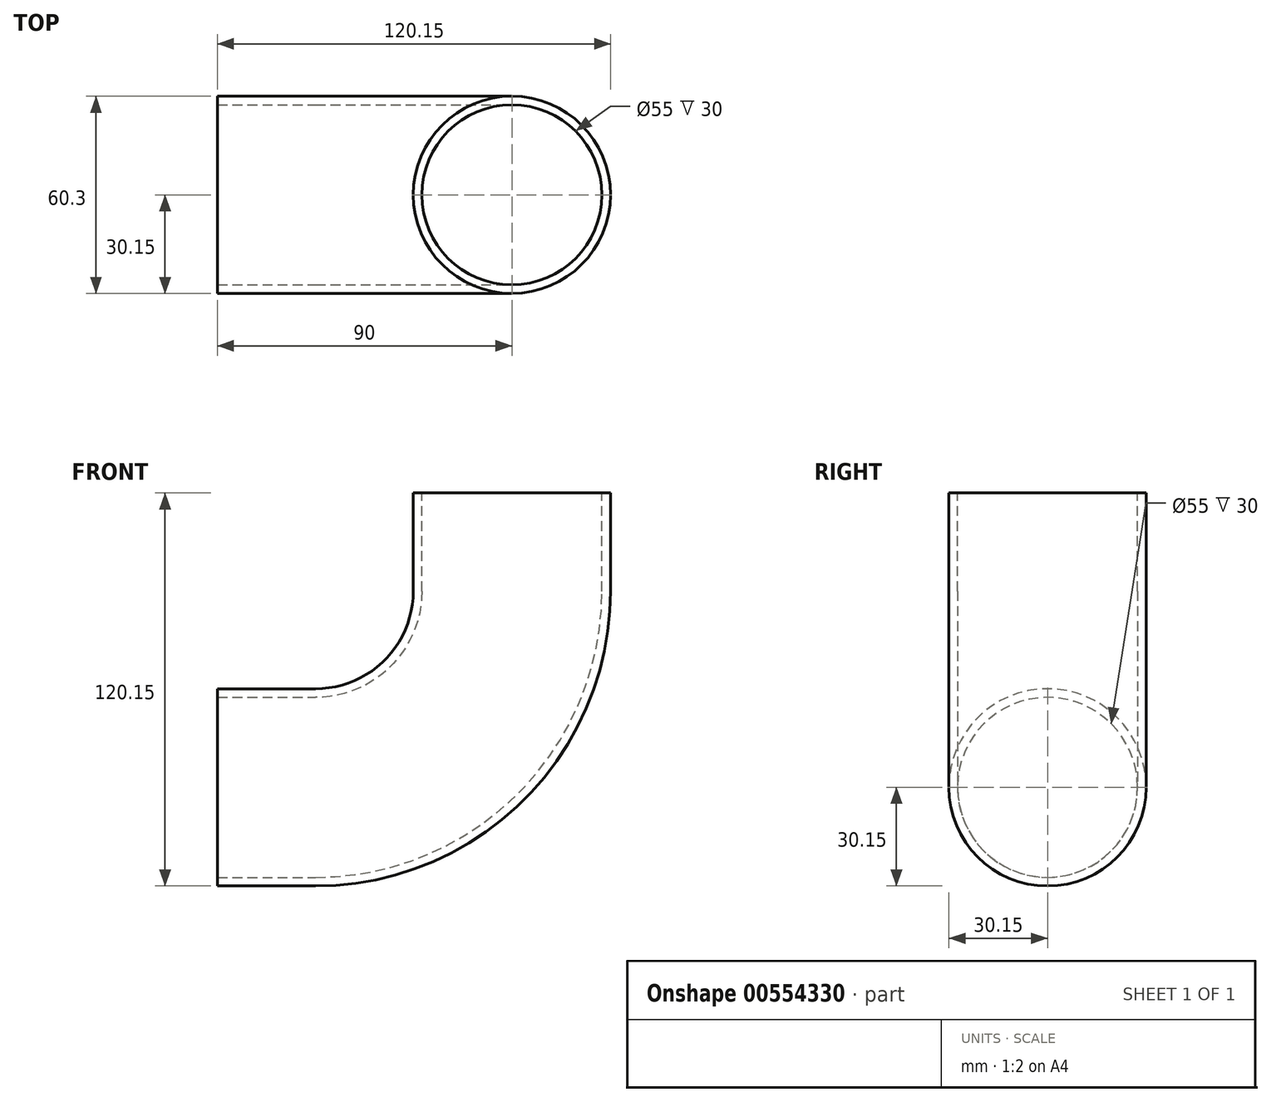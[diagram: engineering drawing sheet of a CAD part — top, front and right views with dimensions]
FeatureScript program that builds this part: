
annotation { "Feature Type Name" : "Feature", "Feature Type Description" : "" }
export const myFeature = defineFeature(function(context is Context, id is Id, definition is map)
    precondition{}
    {
        {
            var Q0;
            Q0=qCreatedBy(makeId("Front.planeOp"),FACE);
            var sketch = newSketch(context, id + "F0", { "sketchPlane" : qUnion([Q0])});
            skLineSegment(sketch, "E0", {"start": v(0, 0) * mm, "end": v(30, 0) * mm});
            skLineSegment(sketch, "E1", {"start": v(90, 60) * mm, "end": v(90, 90) * mm});
            skPoint(sketch, "E2.visualSharp", {"position": v(90, 0) * mm});
            skArc(sketch, "E2.filletArc", {"start": v(30, 0) * mm, "mid": v(72.43, 17.57) * mm, "end": v(90, 60) * mm});
            skSolve(sketch);
        }
        {
            var Q0;
            Q0=qCreatedBy(makeId("Right.planeOp"),FACE);
            var sketch = newSketch(context, id + "F1", { "sketchPlane" : qUnion([Q0])});
            skCircle(sketch, "E3", {"center": v(0, 0) * mm, "radius": 30.15 * mm});
            skCircle(sketch, "E4", {"center": v(0, 0) * mm, "radius": 27.5 * mm});
            skSolve(sketch);
        }
        {
            var Q0;
            Q0=makeQuery(id+"F1.imprint","IMPRINT",FACE,{"disambiguationData":[TD([[makeQuery(id+"F1.imprint","IMPRINT",EDGE,{"derivedFrom":sQuery(id+"F1.wireOp",EDGE,"E3")}),1.0]])]});
            var Q1;
            Q1=sQuery(id+"F0.wireOp",EDGE,"E0");
            var Q2;
            Q2=sQuery(id+"F0.wireOp",EDGE,"E2.filletArc");
            var Q3;
            Q3=sQuery(id+"F0.wireOp",EDGE,"E1");
            sweep(context, id + "F2", {"profiles" : qUnion([Q0]), "path" : qUnion([Q1, Q2, Q3])});
        }
    });
